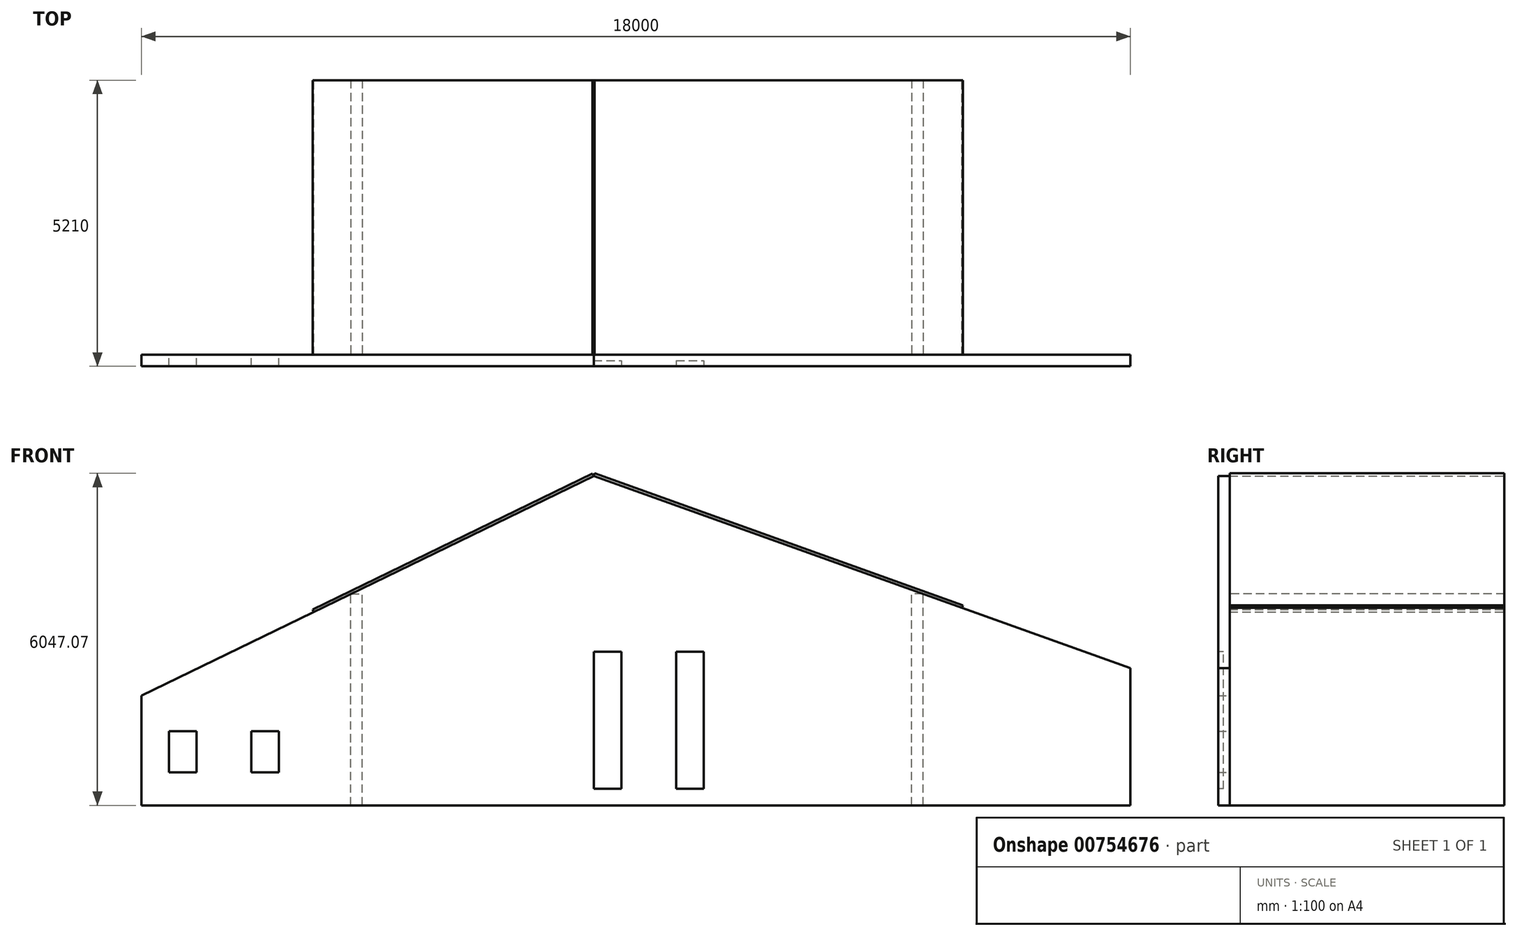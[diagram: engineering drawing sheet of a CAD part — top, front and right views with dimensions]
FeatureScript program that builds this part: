
annotation { "Feature Type Name" : "Feature", "Feature Type Description" : "" }
export const myFeature = defineFeature(function(context is Context, id is Id, definition is map)
    precondition{}
    {
        {
            var Q0;
            Q0=qCreatedBy(makeId("Front.planeOp"),FACE);
            var sketch = newSketch(context, id + "F0", { "sketchPlane" : qUnion([Q0])});
            skLineSegment(sketch, "E0", {"start": v(0, 0) * mm, "end": v(9766.49, 0) * mm});
            skLineSegment(sketch, "E1", {"start": v(9766.49, 0) * mm, "end": v(9766.49, 2500) * mm});
            skLineSegment(sketch, "E2", {"start": v(9766.49, 2500) * mm, "end": v(0, 6000) * mm});
            skLineSegment(sketch, "E3", {"start": v(0, 6000) * mm, "end": v(-5203.54, 3472.02) * mm});
            skLineSegment(sketch, "E4", {"start": v(-5203.54, 3472.02) * mm, "end": v(-8233.51, 2000) * mm});
            skLineSegment(sketch, "E5", {"start": v(-8233.51, 2000) * mm, "end": v(-8233.51, 0) * mm});
            skLineSegment(sketch, "E6", {"start": v(-8233.51, 0) * mm, "end": v(0, 0) * mm});
            skLineSegment(sketch, "E7.bottom", {"start": v(-7733.51, 1350) * mm, "end": v(-7233.51, 1350) * mm});
            skLineSegment(sketch, "E7.top", {"start": v(-7733.51, 600) * mm, "end": v(-7233.51, 600) * mm});
            skLineSegment(sketch, "E7.left", {"start": v(-7733.51, 1350) * mm, "end": v(-7733.51, 600) * mm});
            skLineSegment(sketch, "E7.right", {"start": v(-7233.51, 1350) * mm, "end": v(-7233.51, 600) * mm});
            skLineSegment(sketch, "E8.bottom", {"start": v(-6233.51, 1350) * mm, "end": v(-5733.51, 1350) * mm});
            skLineSegment(sketch, "E8.top", {"start": v(-6233.51, 600) * mm, "end": v(-5733.51, 600) * mm});
            skLineSegment(sketch, "E8.left", {"start": v(-6233.51, 1350) * mm, "end": v(-6233.51, 600) * mm});
            skLineSegment(sketch, "E8.right", {"start": v(-5733.51, 1350) * mm, "end": v(-5733.51, 600) * mm});
            skSolve(sketch);
        }
        {
            var Q0;
            Q0=makeQuery(id+"F0.imprint","IMPRINT",FACE,{"disambiguationData":[TD([[makeQuery(id+"F0.imprint","IMPRINT",EDGE,{"derivedFrom":sQuery(id+"F0.wireOp",EDGE,"E0")}),1.0]])]});
            extrude(context, id + "F1", {"entities" : qUnion([Q0]), "depth" : 210 * mm, "offsetDistance" : 25 * mm});
        }
        {
            var Q0;
            Q0=makeQuery(id+"F1.opExtrude","CAP_FACE",FACE,{"disambiguationData":[OSD([sQuery(id+"F0.wireOp",EDGE,"E0"),sQuery(id+"F0.wireOp",EDGE,"E1"),sQuery(id+"F0.wireOp",EDGE,"E2"),sQuery(id+"F0.wireOp",EDGE,"E3"),sQuery(id+"F0.wireOp",EDGE,"E4"),sQuery(id+"F0.wireOp",EDGE,"E5"),sQuery(id+"F0.wireOp",EDGE,"E6"),sQuery(id+"F0.wireOp",EDGE,"E7.bottom"),sQuery(id+"F0.wireOp",EDGE,"E7.top"),sQuery(id+"F0.wireOp",EDGE,"E7.left"),sQuery(id+"F0.wireOp",EDGE,"E7.right"),sQuery(id+"F0.wireOp",EDGE,"E8.bottom"),sQuery(id+"F0.wireOp",EDGE,"E8.top"),sQuery(id+"F0.wireOp",EDGE,"E8.left"),sQuery(id+"F0.wireOp",EDGE,"E8.right")])],"isStart":false});
            var sketch = newSketch(context, id + "F2", { "sketchPlane" : qUnion([Q0])});
            skLineSegment(sketch, "E9", {"start": v(0, 6000) * mm, "end": v(0, 0) * mm, "construction": true});
            skLineSegment(sketch, "E10.bottom", {"start": v(0, 300) * mm, "end": v(500, 300) * mm});
            skLineSegment(sketch, "E10.top", {"start": v(0, 2800) * mm, "end": v(500, 2800) * mm});
            skLineSegment(sketch, "E10.left", {"start": v(0, 300) * mm, "end": v(0, 2800) * mm});
            skLineSegment(sketch, "E10.right", {"start": v(500, 300) * mm, "end": v(500, 2800) * mm});
            skLineSegment(sketch, "E11.bottom", {"start": v(1500, 300) * mm, "end": v(2000, 300) * mm});
            skLineSegment(sketch, "E11.top", {"start": v(1500, 2800) * mm, "end": v(2000, 2800) * mm});
            skLineSegment(sketch, "E11.left", {"start": v(1500, 300) * mm, "end": v(1500, 2800) * mm});
            skLineSegment(sketch, "E11.right", {"start": v(2000, 300) * mm, "end": v(2000, 2800) * mm});
            skSolve(sketch);
        }
        {
            var Q0;
            Q0=makeQuery(id+"F2.imprint","IMPRINT",FACE,{"disambiguationData":[TD([[makeQuery(id+"F2.imprint","IMPRINT",EDGE,{"derivedFrom":sQuery(id+"F2.wireOp",EDGE,"E10.bottom")}),1.0]])]});
            var Q1;
            Q1=makeQuery(id+"F2.imprint","IMPRINT",FACE,{"disambiguationData":[TD([[makeQuery(id+"F2.imprint","IMPRINT",EDGE,{"derivedFrom":sQuery(id+"F2.wireOp",EDGE,"E11.bottom")}),1.0]])]});
            extrude(context, id + "F3", {"entities" : qUnion([Q0, Q1]), "operationType" : NewBodyOperationType.REMOVE, "oppositeDirection" : true, "depth" : 100 * mm, "offsetDistance" : 25 * mm});
        }
        {
            var Q0;
            Q0=makeQuery(id+"F1.opExtrude","CAP_FACE",FACE,{"disambiguationData":[OSD([sQuery(id+"F0.wireOp",EDGE,"E0"),sQuery(id+"F0.wireOp",EDGE,"E1"),sQuery(id+"F0.wireOp",EDGE,"E2"),sQuery(id+"F0.wireOp",EDGE,"E3"),sQuery(id+"F0.wireOp",EDGE,"E4"),sQuery(id+"F0.wireOp",EDGE,"E5"),sQuery(id+"F0.wireOp",EDGE,"E6"),sQuery(id+"F0.wireOp",EDGE,"E7.bottom"),sQuery(id+"F0.wireOp",EDGE,"E7.top"),sQuery(id+"F0.wireOp",EDGE,"E7.left"),sQuery(id+"F0.wireOp",EDGE,"E7.right"),sQuery(id+"F0.wireOp",EDGE,"E8.bottom"),sQuery(id+"F0.wireOp",EDGE,"E8.top"),sQuery(id+"F0.wireOp",EDGE,"E8.left"),sQuery(id+"F0.wireOp",EDGE,"E8.right")])],"isStart":true});
            var sketch = newSketch(context, id + "F4", { "sketchPlane" : qUnion([Q0])});
            skLineSegment(sketch, "E12.bottom", {"start": v(-5996.58, 0) * mm, "end": v(-5786.58, 0) * mm});
            skLineSegment(sketch, "E12.top", {"start": v(-5996.58, 3851.02) * mm, "end": v(-5786.58, 3851.02) * mm});
            skLineSegment(sketch, "E12.left", {"start": v(-5996.58, 0) * mm, "end": v(-5996.58, 3851.02) * mm});
            skLineSegment(sketch, "E12.right", {"start": v(-5786.58, 0) * mm, "end": v(-5786.58, 3851.02) * mm});
            skLineSegment(sketch, "E13.bottom", {"start": v(4423.42, 0) * mm, "end": v(4213.42, 0) * mm});
            skLineSegment(sketch, "E13.top", {"start": v(4423.42, 3851.02) * mm, "end": v(4213.42, 3851.02) * mm});
            skLineSegment(sketch, "E13.left", {"start": v(4423.42, 0) * mm, "end": v(4423.42, 3851.02) * mm});
            skLineSegment(sketch, "E13.right", {"start": v(4213.42, 0) * mm, "end": v(4213.42, 3851.02) * mm});
            skSolve(sketch);
        }
        {
            var Q0;
            Q0=makeQuery(id+"F4.imprint","IMPRINT",FACE,{"disambiguationData":[TD([[makeQuery(id+"F4.imprint","IMPRINT",EDGE,{"derivedFrom":sQuery(id+"F4.wireOp",EDGE,"E13.bottom")}),-1.0]])]});
            var Q1;
            Q1=makeQuery(id+"F4.imprint","IMPRINT",FACE,{"disambiguationData":[TD([[makeQuery(id+"F4.imprint","IMPRINT",EDGE,{"derivedFrom":sQuery(id+"F4.wireOp",EDGE,"E12.bottom")}),-1.0]])]});
            extrude(context, id + "F5", {"entities" : qUnion([Q0, Q1]), "operationType" : NewBodyOperationType.ADD, "depth" : 5000 * mm, "offsetDistance" : 25 * mm});
        }
        {
            var Q0;
            Q0=makeQuery(id+"F1.opExtrude","SWEPT_FACE",FACE,{"disambiguationData":[OSD([sQuery(id+"F0.wireOp",EDGE,"E3"),sQuery(id+"F0.wireOp",EDGE,"E4")])]});
            var sketch = newSketch(context, id + "F6", { "sketchPlane" : qUnion([Q0])});
            skLineSegment(sketch, "E14.bottom", {"start": v(2621.88, -210) * mm, "end": v(-3045.92, -210) * mm});
            skLineSegment(sketch, "E14.top", {"start": v(2621.88, 5000) * mm, "end": v(-3045.92, 5000) * mm});
            skLineSegment(sketch, "E14.left", {"start": v(2621.88, -210) * mm, "end": v(2621.88, 5000) * mm});
            skLineSegment(sketch, "E14.right", {"start": v(-3045.92, -210) * mm, "end": v(-3045.92, 5000) * mm});
            skSolve(sketch);
        }
        {
            var Q0;
            {var subQ11=sQuery(id+"F6.wireOp",EDGE,"E14.top");Q0=makeQuery(id+"F6.imprint","IMPRINT",FACE,{"disambiguationData":[TD([[makeQuery(id+"F6.imprint","IMPRINT",EDGE,{"derivedFrom":subQ11}),1.0]])]});}
            extrude(context, id + "F7", {"entities" : qUnion([Q0]), "depth" : 50 * mm, "offsetDistance" : 25 * mm});
        }
        {
            var Q0;
            Q0=makeQuery(id+"F1.opExtrude","SWEPT_FACE",FACE,{"disambiguationData":[OSD([sQuery(id+"F0.wireOp",EDGE,"E2")])]});
            var sketch = newSketch(context, id + "F8", { "sketchPlane" : qUnion([Q0])});
            skLineSegment(sketch, "E15.bottom", {"start": v(-2024.16, 0) * mm, "end": v(5095.86, 0) * mm});
            skLineSegment(sketch, "E15.top", {"start": v(-2024.16, 5000) * mm, "end": v(5095.86, 5000) * mm});
            skLineSegment(sketch, "E15.left", {"start": v(-2024.16, 0) * mm, "end": v(-2024.16, 5000) * mm});
            skLineSegment(sketch, "E15.right", {"start": v(5095.86, 0) * mm, "end": v(5095.86, 5000) * mm});
            skSolve(sketch);
        }
        {
            var Q0;
            Q0=makeQuery(id+"F8.imprint","IMPRINT",FACE,{"disambiguationData":[TD([[makeQuery(id+"F8.imprint","IMPRINT",EDGE,{"derivedFrom":sQuery(id+"F8.wireOp",EDGE,"E15.top")}),-1.0]])]});
            extrude(context, id + "F9", {"entities" : qUnion([Q0]), "depth" : 50 * mm, "offsetDistance" : 25 * mm});
        }
    });
